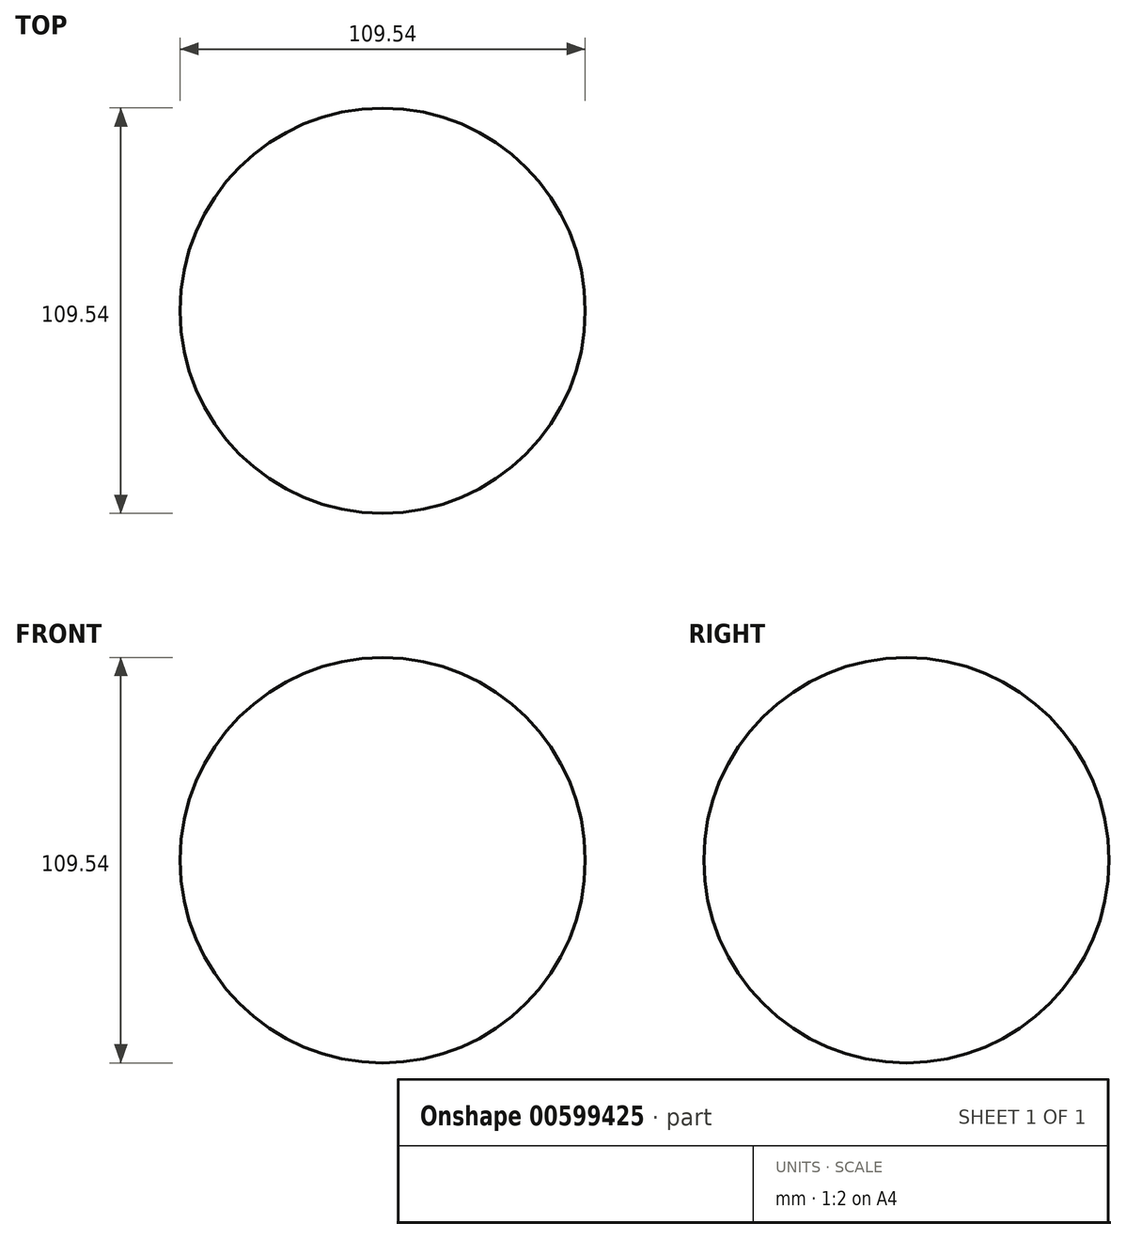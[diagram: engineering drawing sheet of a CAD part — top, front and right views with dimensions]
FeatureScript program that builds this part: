
annotation { "Feature Type Name" : "Feature", "Feature Type Description" : "" }
export const myFeature = defineFeature(function(context is Context, id is Id, definition is map)
    precondition{}
    {
        {
            var Q0;
            Q0=qCreatedBy(makeId("Front.planeOp"),FACE);
            var sketch = newSketch(context, id + "F0", { "sketchPlane" : qUnion([Q0])});
            skArc(sketch, "E0", {"start": v(54.77, 0) * mm, "mid": v(38.73, 38.73) * mm, "end": v(0, 54.77) * mm});
            skArc(sketch, "E1", {"start": v(0, 54.77) * mm, "mid": v(-38.73, 38.73) * mm, "end": v(-54.77, 0) * mm});
            skLineSegment(sketch, "E2", {"start": v(-54.77, 0) * mm, "end": v(0, 0) * mm});
            skLineSegment(sketch, "E3", {"start": v(0, 0) * mm, "end": v(54.77, 0) * mm});
            skSolve(sketch);
        }
        {
            var Q0;
            Q0=makeQuery(id+"F0.imprint","IMPRINT",FACE,{"disambiguationData":[TD([[makeQuery(id+"F0.imprint","IMPRINT",EDGE,{"derivedFrom":sQuery(id+"F0.wireOp",EDGE,"E0")}),1.0]])]});
            var Q1;
            Q1=sQuery(id+"F0.wireOp",EDGE,"E2");
            revolve(context, id + "F1", {"entities" : qUnion([Q0]), "axis" : qUnion([Q1]), "revolveType" : RevolveType.FULL});
        }
    });
